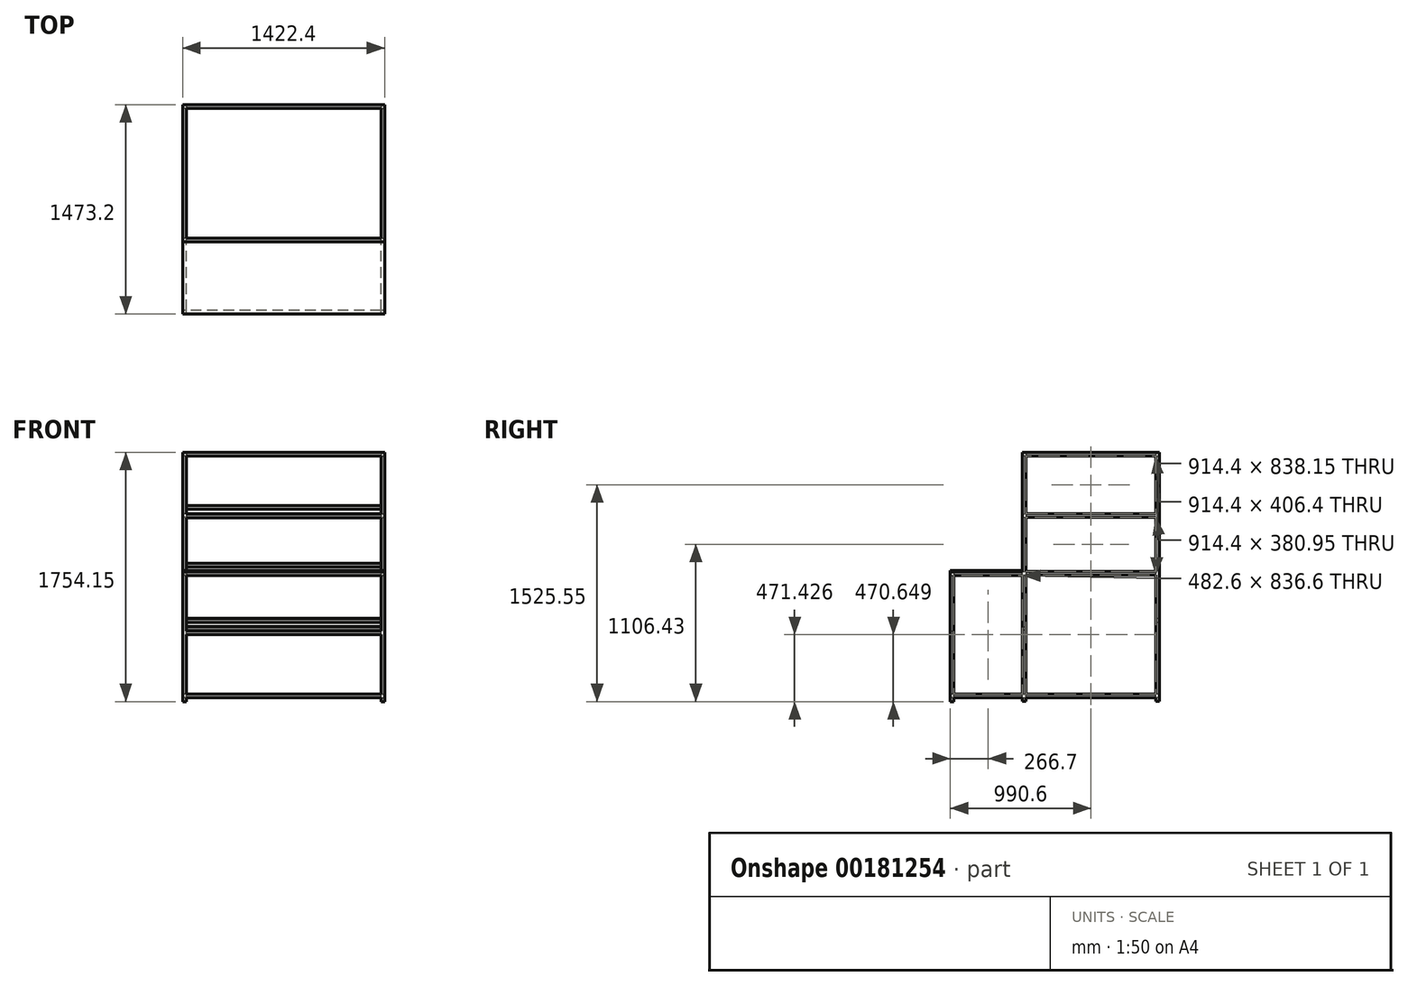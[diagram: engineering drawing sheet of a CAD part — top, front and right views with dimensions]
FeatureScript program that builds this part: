
annotation { "Feature Type Name" : "Feature", "Feature Type Description" : "" }
export const myFeature = defineFeature(function(context is Context, id is Id, definition is map)
    precondition{}
    {
        {
            var Q0;
            Q0=qCreatedBy(makeId("Top.planeOp"),FACE);
            var sketch = newSketch(context, id + "F0", { "sketchPlane" : qUnion([Q0])});
            skLineSegment(sketch, "E0.bottom", {"start": v(685.8, 457.2) * mm, "end": v(-685.8, 457.2) * mm});
            skLineSegment(sketch, "E0.top", {"start": v(685.8, -457.2) * mm, "end": v(-685.8, -457.2) * mm});
            skLineSegment(sketch, "E0.left", {"start": v(685.8, 457.2) * mm, "end": v(685.8, -457.2) * mm});
            skLineSegment(sketch, "E0.right", {"start": v(-685.8, 457.2) * mm, "end": v(-685.8, -457.2) * mm});
            skPoint(sketch, "E0.middle", {"position": v(0, 0) * mm});
            skLineSegment(sketch, "E1.bottom", {"start": v(711.2, 482.6) * mm, "end": v(-711.2, 482.6) * mm});
            skLineSegment(sketch, "E1.top", {"start": v(711.2, -482.6) * mm, "end": v(-711.2, -482.6) * mm});
            skLineSegment(sketch, "E1.left", {"start": v(711.2, 482.6) * mm, "end": v(711.2, -482.6) * mm});
            skLineSegment(sketch, "E1.right", {"start": v(-711.2, 482.6) * mm, "end": v(-711.2, -482.6) * mm});
            skLineSegment(sketch, "E2.bottom", {"start": v(-685.8, 457.2) * mm, "end": v(-711.2, 457.2) * mm});
            skLineSegment(sketch, "E2.top", {"start": v(-685.8, 482.6) * mm, "end": v(-711.2, 482.6) * mm});
            skLineSegment(sketch, "E2.left", {"start": v(-685.8, 457.2) * mm, "end": v(-685.8, 482.6) * mm});
            skLineSegment(sketch, "E2.right", {"start": v(-711.2, 457.2) * mm, "end": v(-711.2, 482.6) * mm});
            skLineSegment(sketch, "E3.bottom", {"start": v(-685.8, -457.2) * mm, "end": v(-711.2, -457.2) * mm});
            skLineSegment(sketch, "E3.top", {"start": v(-685.8, -482.6) * mm, "end": v(-711.2, -482.6) * mm});
            skLineSegment(sketch, "E3.left", {"start": v(-685.8, -457.2) * mm, "end": v(-685.8, -482.6) * mm});
            skLineSegment(sketch, "E3.right", {"start": v(-711.2, -457.2) * mm, "end": v(-711.2, -482.6) * mm});
            skLineSegment(sketch, "E4.bottom", {"start": v(685.8, -457.2) * mm, "end": v(711.2, -457.2) * mm});
            skLineSegment(sketch, "E4.top", {"start": v(685.8, -482.6) * mm, "end": v(711.2, -482.6) * mm});
            skLineSegment(sketch, "E4.left", {"start": v(685.8, -457.2) * mm, "end": v(685.8, -482.6) * mm});
            skLineSegment(sketch, "E4.right", {"start": v(711.2, -457.2) * mm, "end": v(711.2, -482.6) * mm});
            skLineSegment(sketch, "E5.bottom", {"start": v(685.8, 457.2) * mm, "end": v(711.2, 457.2) * mm});
            skLineSegment(sketch, "E5.top", {"start": v(685.8, 482.6) * mm, "end": v(711.2, 482.6) * mm});
            skLineSegment(sketch, "E5.left", {"start": v(685.8, 457.2) * mm, "end": v(685.8, 482.6) * mm});
            skLineSegment(sketch, "E5.right", {"start": v(711.2, 457.2) * mm, "end": v(711.2, 482.6) * mm});
            skSolve(sketch);
        }
        {
            var Q0;
            Q0 = qSketchRegion(id + "F0", true);
            extrude(context, id + "F1", {"entities" : qUnion([Q0]), "depth" : 25.4 * mm});
        }
        {
            var Q0;
            Q0=makeQuery(id+"F0.imprint","IMPRINT",FACE,{"disambiguationData":[TD([[makeQuery(id+"F0.imprint","IMPRINT",EDGE,{"derivedFrom":sQuery(id+"F0.wireOp",EDGE,"E3.bottom")}),1.0]])]});
            var Q1;
            Q1=makeQuery(id+"F0.imprint","IMPRINT",FACE,{"disambiguationData":[TD([[makeQuery(id+"F0.imprint","IMPRINT",EDGE,{"derivedFrom":sQuery(id+"F0.wireOp",EDGE,"E2.bottom")}),-1.0]])]});
            var Q2;
            Q2=makeQuery(id+"F0.imprint","IMPRINT",FACE,{"disambiguationData":[TD([[makeQuery(id+"F0.imprint","IMPRINT",EDGE,{"derivedFrom":sQuery(id+"F0.wireOp",EDGE,"E5.bottom")}),1.0]])]});
            var Q3;
            Q3=makeQuery(id+"F0.imprint","IMPRINT",FACE,{"disambiguationData":[TD([[makeQuery(id+"F0.imprint","IMPRINT",EDGE,{"derivedFrom":sQuery(id+"F0.wireOp",EDGE,"E4.bottom")}),-1.0]])]});
            extrude(context, id + "F2", {"entities" : qUnion([Q0, Q1, Q2, Q3]), "operationType" : NewBodyOperationType.ADD, "oppositeDirection" : true, "depth" : 1727.2 * mm});
        }
        {
            var Q0;
            {var subQ0=sQuery(id+"F0.wireOp",EDGE,"E5.right");var subQ1=sQuery(id+"F0.wireOp",EDGE,"E4.right");Q0=makeQuery(id+"F2.boolean.opBoolean","MERGE",FACE,{"derivedFrom":[makeQuery(id+"F1.opExtrude","SWEPT_FACE",FACE,{"disambiguationData":[OSD([sQuery(id+"F0.wireOp",EDGE,"E1.left"),subQ1,subQ0])]}),makeQuery(id+"F2.opExtrude","SWEPT_FACE",FACE,{"disambiguationData":[OSD([subQ1])]}),makeQuery(id+"F2.opExtrude","SWEPT_FACE",FACE,{"disambiguationData":[OSD([subQ0])]})]});}
            var sketch = newSketch(context, id + "F3", { "sketchPlane" : qUnion([Q0])});
            skLineSegment(sketch, "E6", {"start": v(-457.2, 0) * mm, "end": v(-457.2, -406.4) * mm});
            skLineSegment(sketch, "E7", {"start": v(-457.2, -406.4) * mm, "end": v(457.2, -350.47) * mm});
            skLineSegment(sketch, "E8", {"start": v(-457.2, 0) * mm, "end": v(457.2, 0) * mm});
            skLineSegment(sketch, "E9", {"start": v(-457.2, -406.4) * mm, "end": v(-482.6, -407.95) * mm});
            skLineSegment(sketch, "E10", {"start": v(-482.6, -407.95) * mm, "end": v(-482.6, -433.4) * mm});
            skLineSegment(sketch, "E11", {"start": v(-482.6, -433.4) * mm, "end": v(457.2, -375.92) * mm});
            skLineSegment(sketch, "E12", {"start": v(457.2, -375.92) * mm, "end": v(482.6, -374.37) * mm});
            skLineSegment(sketch, "E13", {"start": v(457.2, -350.47) * mm, "end": v(482.6, -348.92) * mm});
            skLineSegment(sketch, "E14", {"start": v(482.6, -348.92) * mm, "end": v(482.6, -374.37) * mm});
            skLineSegment(sketch, "E15.1.0.0", {"start": v(-457.2, -812.8) * mm, "end": v(457.2, -756.87) * mm});
            skLineSegment(sketch, "E15.1.0.1", {"start": v(-482.6, -839.8) * mm, "end": v(457.2, -782.32) * mm});
            skLineSegment(sketch, "E15.1.0.2", {"start": v(457.2, -782.32) * mm, "end": v(482.6, -780.77) * mm});
            skLineSegment(sketch, "E15.1.0.3", {"start": v(482.6, -755.32) * mm, "end": v(482.6, -780.77) * mm});
            skLineSegment(sketch, "E15.1.0.4", {"start": v(-482.6, -814.35) * mm, "end": v(-482.6, -839.8) * mm});
            skLineSegment(sketch, "E15.1.0.5", {"start": v(-457.2, -812.8) * mm, "end": v(-482.6, -814.35) * mm});
            skLineSegment(sketch, "E15.1.0.6", {"start": v(457.2, -756.87) * mm, "end": v(482.6, -755.32) * mm});
            skLineSegment(sketch, "E15.direction1", {"start": v(-482.6, -433.4) * mm, "end": v(-482.6, -839.8) * mm, "construction": true});
            skSolve(sketch);
        }
        {
            var Q0;
            {var subQ0=sQuery(id+"F3.wireOp",EDGE,"E9");Q0=makeQuery(id+"F3.imprint","IMPRINT",FACE,{"disambiguationData":[TD([[makeQuery(id+"F3.imprint","IMPRINT",EDGE,{"derivedFrom":subQ0}),1.0]])]});}
            var Q1;
            {var subQ0=sQuery(id+"F3.wireOp",EDGE,"E12");Q1=makeQuery(id+"F3.imprint","IMPRINT",FACE,{"disambiguationData":[TD([[makeQuery(id+"F3.imprint","IMPRINT",EDGE,{"derivedFrom":subQ0}),1.0]])]});}
            var Q2;
            {var subQ0=sQuery(id+"F3.wireOp",EDGE,"E15.1.0.2");Q2=makeQuery(id+"F3.imprint","IMPRINT",FACE,{"disambiguationData":[TD([[makeQuery(id+"F3.imprint","IMPRINT",EDGE,{"derivedFrom":subQ0}),1.0]])]});}
            var Q3;
            {var subQ0=sQuery(id+"F3.wireOp",EDGE,"E15.1.0.4");Q3=makeQuery(id+"F3.imprint","IMPRINT",FACE,{"disambiguationData":[TD([[makeQuery(id+"F3.imprint","IMPRINT",EDGE,{"derivedFrom":subQ0}),1.0]])]});}
            extrude(context, id + "F4", {"entities" : qUnion([Q0, Q1, Q2, Q3]), "operationType" : NewBodyOperationType.ADD, "oppositeDirection" : true, "depth" : 1422.4 * mm});
        }
        {
            var Q0;
            Q0=qCreatedBy(makeId("Top.planeOp"),FACE);
            cPlane(context, id + "F5", {"entities" : qUnion([Q0]), "cplaneType" : CPlaneType.OFFSET, "offset" : 1676.4 * mm, "oppositeDirection" : true, "width" : 152.4 * mm, "height" : 152.4 * mm});
        }
        {
            var Q0;
            Q0=qCreatedBy(id+"F5.planeOp",FACE);
            var sketch = newSketch(context, id + "F6", { "sketchPlane" : qUnion([Q0])});
            skLineSegment(sketch, "E16.bottom", {"start": v(-711.2, -482.6) * mm, "end": v(711.2, -482.6) * mm});
            skLineSegment(sketch, "E16.top", {"start": v(-711.2, 482.6) * mm, "end": v(711.2, 482.6) * mm});
            skLineSegment(sketch, "E16.left", {"start": v(-711.2, -482.6) * mm, "end": v(-711.2, 482.6) * mm});
            skLineSegment(sketch, "E16.right", {"start": v(711.2, -482.6) * mm, "end": v(711.2, 482.6) * mm});
            skPoint(sketch, "E16.middle", {"position": v(0, 0) * mm});
            skLineSegment(sketch, "E17.bottom", {"start": v(-685.8, -457.2) * mm, "end": v(685.8, -457.2) * mm});
            skLineSegment(sketch, "E17.top", {"start": v(-685.8, 457.2) * mm, "end": v(685.8, 457.2) * mm});
            skLineSegment(sketch, "E17.left", {"start": v(-685.8, -457.2) * mm, "end": v(-685.8, 457.2) * mm});
            skLineSegment(sketch, "E17.right", {"start": v(685.8, -457.2) * mm, "end": v(685.8, 457.2) * mm});
            skSolve(sketch);
        }
        {
            var Q0;
            Q0 = qSketchRegion(id + "F6", true);
            extrude(context, id + "F7", {"entities" : qUnion([Q0]), "operationType" : NewBodyOperationType.ADD, "oppositeDirection" : true, "depth" : 25.4 * mm});
        }
        {
            var Q0;
            {var subQ2=sQuery(id+"F3.wireOp",EDGE,"E11");var subQ7=sQuery(id+"F0.wireOp",EDGE,"E4.right");var subQ8=sQuery(id+"F0.wireOp",EDGE,"E1.left");var subQ11=sQuery(id+"F0.wireOp",EDGE,"E0.top");var subQ14=sQuery(id+"F3.wireOp",EDGE,"E15.1.0.1");var subQ18=sQuery(id+"F0.wireOp",EDGE,"E4.bottom");var subQ19=makeQuery(id+"F2.opExtrude","SWEPT_EDGE",EDGE,{"disambiguationData":[OSD([subQ8,subQ18,subQ7])]});Q0=makeQuery(id+"F7.boolean.opBoolean","SPLIT",FACE,{"disambiguationData":[TD([makeQuery(id+"F1.opExtrude","SWEPT_FACE",FACE,{"disambiguationData":[OSD([subQ11])]})])],"derivedFrom":makeQuery(id+"F4.boolean.opBoolean","MERGE",FACE,{"derivedFrom":[makeQuery(id+"F2.opExtrude","SWEPT_FACE",FACE,{"disambiguationData":[OSD([sQuery(id+"F0.wireOp",EDGE,"E3.bottom")])]}),makeQuery(id+"F2.opExtrude","SWEPT_FACE",FACE,{"disambiguationData":[OSD([subQ18])]}),makeQuery(id+"F4.opExtrude","SWEPT_FACE",FACE,{"disambiguationData":[OSD([subQ8,subQ18,subQ7]),TDD([makeQuery(id+"F3.imprint","IMPRINT",EDGE,{"disambiguationData":[TD([[makeQuery(id+"F3.imprint","INTERSECT",VERTEX,{"derivedFrom":[subQ19,subQ2]}),-1.0]])],"derivedFrom":subQ19})])]}),makeQuery(id+"F4.opExtrude","SWEPT_FACE",FACE,{"disambiguationData":[OSD([subQ8,subQ18,subQ7]),TDD([makeQuery(id+"F3.imprint","IMPRINT",EDGE,{"disambiguationData":[TD([[makeQuery(id+"F3.imprint","INTERSECT",VERTEX,{"derivedFrom":[subQ19,subQ14]}),-1.0]])],"derivedFrom":subQ19})])]})]})});}
            var sketch = newSketch(context, id + "F8", { "sketchPlane" : qUnion([Q0])});
            skLineSegment(sketch, "E18.bottom", {"start": v(-685.8, -812.8) * mm, "end": v(-711.2, -812.8) * mm});
            skLineSegment(sketch, "E18.top", {"start": v(-685.8, -838.25) * mm, "end": v(-711.2, -838.25) * mm});
            skLineSegment(sketch, "E18.left", {"start": v(-685.8, -812.8) * mm, "end": v(-685.8, -838.25) * mm});
            skLineSegment(sketch, "E18.right", {"start": v(-711.2, -812.8) * mm, "end": v(-711.2, -838.25) * mm});
            skLineSegment(sketch, "E19.bottom", {"start": v(685.8, -812.8) * mm, "end": v(711.2, -812.8) * mm});
            skLineSegment(sketch, "E19.top", {"start": v(685.8, -838.25) * mm, "end": v(711.2, -838.25) * mm});
            skLineSegment(sketch, "E19.left", {"start": v(685.8, -812.8) * mm, "end": v(685.8, -838.25) * mm});
            skLineSegment(sketch, "E19.right", {"start": v(711.2, -812.8) * mm, "end": v(711.2, -838.25) * mm});
            skLineSegment(sketch, "E20.bottom", {"start": v(-685.8, -406.4) * mm, "end": v(-711.2, -406.4) * mm});
            skLineSegment(sketch, "E20.top", {"start": v(-685.8, -431.85) * mm, "end": v(-711.2, -431.85) * mm});
            skLineSegment(sketch, "E20.left", {"start": v(-685.8, -406.4) * mm, "end": v(-685.8, -431.85) * mm});
            skLineSegment(sketch, "E20.right", {"start": v(-711.2, -406.4) * mm, "end": v(-711.2, -431.85) * mm});
            skLineSegment(sketch, "E21.bottom", {"start": v(685.8, -406.4) * mm, "end": v(711.2, -406.4) * mm});
            skLineSegment(sketch, "E21.top", {"start": v(685.8, -431.85) * mm, "end": v(711.2, -431.85) * mm});
            skLineSegment(sketch, "E21.left", {"start": v(685.8, -406.4) * mm, "end": v(685.8, -431.85) * mm});
            skLineSegment(sketch, "E21.right", {"start": v(711.2, -406.4) * mm, "end": v(711.2, -431.85) * mm});
            skSolve(sketch);
        }
        {
            var Q0;
            Q0 = qSketchRegion(id + "F8", true);
            extrude(context, id + "F9", {"entities" : qUnion([Q0]), "operationType" : NewBodyOperationType.ADD, "depth" : 914.4 * mm});
        }
        {
            var Q0;
            {var subQ0=sQuery(id+"F0.wireOp",EDGE,"E4.top");var subQ1=sQuery(id+"F0.wireOp",EDGE,"E3.top");Q0=makeQuery(id+"F7.boolean.opBoolean","MERGE",FACE,{"derivedFrom":[makeQuery(id+"F4.boolean.opBoolean","MERGE",FACE,{"derivedFrom":[makeQuery(id+"F2.boolean.opBoolean","MERGE",FACE,{"derivedFrom":[makeQuery(id+"F1.opExtrude","SWEPT_FACE",FACE,{"disambiguationData":[OSD([sQuery(id+"F0.wireOp",EDGE,"E1.top"),subQ1,subQ0])]}),makeQuery(id+"F2.opExtrude","SWEPT_FACE",FACE,{"disambiguationData":[OSD([subQ1])]}),makeQuery(id+"F2.opExtrude","SWEPT_FACE",FACE,{"disambiguationData":[OSD([subQ0])]})]}),makeQuery(id+"F4.opExtrude","SWEPT_FACE",FACE,{"disambiguationData":[OSD([sQuery(id+"F3.wireOp",EDGE,"E10")])]}),makeQuery(id+"F4.opExtrude","SWEPT_FACE",FACE,{"disambiguationData":[OSD([sQuery(id+"F3.wireOp",EDGE,"E15.1.0.4")])]})]}),makeQuery(id+"F7.opExtrude","SWEPT_FACE",FACE,{"disambiguationData":[OSD([sQuery(id+"F6.wireOp",EDGE,"E16.bottom")])]})]});}
            var sketch = newSketch(context, id + "F10", { "sketchPlane" : qUnion([Q0])});
            skLineSegment(sketch, "E22.bottom", {"start": v(-685.8, -839.8) * mm, "end": v(-711.2, -839.8) * mm});
            skLineSegment(sketch, "E22.top", {"start": v(-685.8, -814.35) * mm, "end": v(-711.2, -814.35) * mm});
            skLineSegment(sketch, "E22.left", {"start": v(-685.8, -839.8) * mm, "end": v(-685.8, -814.35) * mm});
            skLineSegment(sketch, "E22.right", {"start": v(-711.2, -839.8) * mm, "end": v(-711.2, -814.35) * mm});
            skLineSegment(sketch, "E23.bottom", {"start": v(685.8, -839.8) * mm, "end": v(711.2, -839.8) * mm});
            skLineSegment(sketch, "E23.top", {"start": v(685.8, -814.35) * mm, "end": v(711.2, -814.35) * mm});
            skLineSegment(sketch, "E23.left", {"start": v(685.8, -839.8) * mm, "end": v(685.8, -814.35) * mm});
            skLineSegment(sketch, "E23.right", {"start": v(711.2, -839.8) * mm, "end": v(711.2, -814.35) * mm});
            skLineSegment(sketch, "E24.bottom", {"start": v(-685.8, -1701.8) * mm, "end": v(-711.2, -1701.8) * mm});
            skLineSegment(sketch, "E24.top", {"start": v(-685.8, -1676.4) * mm, "end": v(-711.2, -1676.4) * mm});
            skLineSegment(sketch, "E24.left", {"start": v(-685.8, -1701.8) * mm, "end": v(-685.8, -1676.4) * mm});
            skLineSegment(sketch, "E24.right", {"start": v(-711.2, -1701.8) * mm, "end": v(-711.2, -1676.4) * mm});
            skLineSegment(sketch, "E25.bottom", {"start": v(685.8, -1701.8) * mm, "end": v(711.2, -1701.8) * mm});
            skLineSegment(sketch, "E25.top", {"start": v(685.8, -1676.4) * mm, "end": v(711.2, -1676.4) * mm});
            skLineSegment(sketch, "E25.left", {"start": v(685.8, -1701.8) * mm, "end": v(685.8, -1676.4) * mm});
            skLineSegment(sketch, "E25.right", {"start": v(711.2, -1701.8) * mm, "end": v(711.2, -1676.4) * mm});
            skSolve(sketch);
        }
        {
            var Q0;
            Q0 = qSketchRegion(id + "F10", true);
            extrude(context, id + "F11", {"entities" : qUnion([Q0]), "operationType" : NewBodyOperationType.ADD, "depth" : 508 * mm});
        }
        {
            var Q0;
            Q0=makeQuery(id+"F11.opExtrude","SWEPT_FACE",FACE,{"disambiguationData":[OSD([sQuery(id+"F10.wireOp",EDGE,"E22.top")])]});
            var sketch = newSketch(context, id + "F12", { "sketchPlane" : qUnion([Q0])});
            skLineSegment(sketch, "E26.bottom", {"start": v(-711.2, -990.6) * mm, "end": v(-685.8, -990.6) * mm});
            skLineSegment(sketch, "E26.top", {"start": v(-711.2, -965.2) * mm, "end": v(-685.8, -965.2) * mm});
            skLineSegment(sketch, "E26.left", {"start": v(-711.2, -990.6) * mm, "end": v(-711.2, -965.2) * mm});
            skLineSegment(sketch, "E26.right", {"start": v(-685.8, -990.6) * mm, "end": v(-685.8, -965.2) * mm});
            skSolve(sketch);
        }
        {
            var Q0;
            Q0 = qSketchRegion(id + "F12", true);
            var Q1;
            Q1 = qSketchRegion(id + "F14", true);
            extrude(context, id + "F13", {"entities" : qUnion([Q0, Q1]), "operationType" : NewBodyOperationType.ADD, "oppositeDirection" : true, "depth" : 914.4 * mm});
        }
        {
            var Q0;
            Q0=makeQuery(id+"F11.opExtrude","SWEPT_FACE",FACE,{"disambiguationData":[OSD([sQuery(id+"F10.wireOp",EDGE,"E23.top")])]});
            var sketch = newSketch(context, id + "F14", { "sketchPlane" : qUnion([Q0])});
            skLineSegment(sketch, "E27.bottom", {"start": v(711.2, -990.6) * mm, "end": v(685.8, -990.6) * mm});
            skLineSegment(sketch, "E27.top", {"start": v(711.2, -965.2) * mm, "end": v(685.8, -965.2) * mm});
            skLineSegment(sketch, "E27.left", {"start": v(711.2, -990.6) * mm, "end": v(711.2, -965.2) * mm});
            skLineSegment(sketch, "E27.right", {"start": v(685.8, -990.6) * mm, "end": v(685.8, -965.2) * mm});
            skSolve(sketch);
        }
        {
            var Q0;
            Q0=makeQuery(id+"F14.imprint","IMPRINT",FACE,{"disambiguationData":[TD([[makeQuery(id+"F14.imprint","IMPRINT",EDGE,{"derivedFrom":sQuery(id+"F14.wireOp",EDGE,"E27.bottom")}),1.0]])]});
            extrude(context, id + "F15", {"entities" : qUnion([Q0]), "operationType" : NewBodyOperationType.ADD, "oppositeDirection" : true, "depth" : 914.4 * mm});
        }
        {
            var Q0;
            Q0=makeQuery(id+"F13.boolean.opBoolean","MERGE",FACE,{"derivedFrom":[makeQuery(id+"F11.opExtrude","SWEPT_FACE",FACE,{"disambiguationData":[OSD([sQuery(id+"F10.wireOp",EDGE,"E22.left")])]}),makeQuery(id+"F11.opExtrude","SWEPT_FACE",FACE,{"disambiguationData":[OSD([sQuery(id+"F10.wireOp",EDGE,"E24.left")])]}),makeQuery(id+"F13.opExtrude","SWEPT_FACE",FACE,{"disambiguationData":[OSD([sQuery(id+"F12.wireOp",EDGE,"E26.right")])]})]});
            var sketch = newSketch(context, id + "F16", { "sketchPlane" : qUnion([Q0])});
            skLineSegment(sketch, "E28.bottom", {"start": v(-990.6, -814.35) * mm, "end": v(-965.2, -814.35) * mm});
            skLineSegment(sketch, "E28.top", {"start": v(-990.6, -839.8) * mm, "end": v(-965.2, -839.8) * mm});
            skLineSegment(sketch, "E28.left", {"start": v(-990.6, -814.35) * mm, "end": v(-990.6, -839.8) * mm});
            skLineSegment(sketch, "E28.right", {"start": v(-965.2, -814.35) * mm, "end": v(-965.2, -839.8) * mm});
            skLineSegment(sketch, "E29.bottom", {"start": v(-965.2, -1701.8) * mm, "end": v(-990.6, -1701.8) * mm});
            skLineSegment(sketch, "E29.top", {"start": v(-965.2, -1676.4) * mm, "end": v(-990.6, -1676.4) * mm});
            skLineSegment(sketch, "E29.left", {"start": v(-965.2, -1701.8) * mm, "end": v(-965.2, -1676.4) * mm});
            skLineSegment(sketch, "E29.right", {"start": v(-990.6, -1701.8) * mm, "end": v(-990.6, -1676.4) * mm});
            skSolve(sketch);
        }
        {
            var Q0;
            Q0 = qSketchRegion(id + "F16", true);
            extrude(context, id + "F17", {"entities" : qUnion([Q0]), "operationType" : NewBodyOperationType.ADD, "depth" : 1371.6 * mm});
        }
        {
            var Q0;
            Q0=makeQuery(id+"F17.boolean.opBoolean","MERGE",FACE,{"derivedFrom":[makeQuery(id+"F11.opExtrude","SWEPT_FACE",FACE,{"disambiguationData":[OSD([sQuery(id+"F10.wireOp",EDGE,"E22.top")])]}),makeQuery(id+"F11.opExtrude","SWEPT_FACE",FACE,{"disambiguationData":[OSD([sQuery(id+"F10.wireOp",EDGE,"E23.top")])]}),makeQuery(id+"F17.opExtrude","SWEPT_FACE",FACE,{"disambiguationData":[OSD([sQuery(id+"F16.wireOp",EDGE,"E28.bottom")])]})]});
            var sketch = newSketch(context, id + "F18", { "sketchPlane" : qUnion([Q0])});
            skLineSegment(sketch, "E30.bottom", {"start": v(-711.2, -990.6) * mm, "end": v(711.2, -990.6) * mm});
            skLineSegment(sketch, "E30.top", {"start": v(-711.2, -482.6) * mm, "end": v(711.2, -482.6) * mm});
            skLineSegment(sketch, "E30.left", {"start": v(-711.2, -990.6) * mm, "end": v(-711.2, -482.6) * mm});
            skLineSegment(sketch, "E30.right", {"start": v(711.2, -990.6) * mm, "end": v(711.2, -482.6) * mm});
            skSolve(sketch);
        }
        {
            var Q0;
            Q0 = qSketchRegion(id + "F18", true);
            extrude(context, id + "F19", {"entities" : qUnion([Q0]), "depth" : 9.52 * mm});
        }
        {
            var Q0;
            {var subQ0=sQuery(id+"F0.wireOp",EDGE,"E5.right");var subQ1=sQuery(id+"F0.wireOp",EDGE,"E4.right");Q0=makeQuery(id+"F15.boolean.opBoolean","MERGE",FACE,{"derivedFrom":[makeQuery(id+"F11.boolean.opBoolean","MERGE",FACE,{"derivedFrom":[makeQuery(id+"F9.boolean.opBoolean","MERGE",FACE,{"derivedFrom":[makeQuery(id+"F7.boolean.opBoolean","MERGE",FACE,{"derivedFrom":[makeQuery(id+"F2.boolean.opBoolean","MERGE",FACE,{"derivedFrom":[makeQuery(id+"F1.opExtrude","SWEPT_FACE",FACE,{"disambiguationData":[OSD([sQuery(id+"F0.wireOp",EDGE,"E1.left"),subQ1,subQ0])]}),makeQuery(id+"F2.opExtrude","SWEPT_FACE",FACE,{"disambiguationData":[OSD([subQ1])]}),makeQuery(id+"F2.opExtrude","SWEPT_FACE",FACE,{"disambiguationData":[OSD([subQ0])]})]}),makeQuery(id+"F7.opExtrude","SWEPT_FACE",FACE,{"disambiguationData":[OSD([sQuery(id+"F6.wireOp",EDGE,"E16.right")])]})]}),makeQuery(id+"F9.opExtrude","SWEPT_FACE",FACE,{"disambiguationData":[OSD([sQuery(id+"F8.wireOp",EDGE,"E18.right")])]}),makeQuery(id+"F9.opExtrude","SWEPT_FACE",FACE,{"disambiguationData":[OSD([sQuery(id+"F8.wireOp",EDGE,"E20.right")])]})]}),makeQuery(id+"F11.opExtrude","SWEPT_FACE",FACE,{"disambiguationData":[OSD([sQuery(id+"F10.wireOp",EDGE,"E23.right")])]}),makeQuery(id+"F11.opExtrude","SWEPT_FACE",FACE,{"disambiguationData":[OSD([sQuery(id+"F10.wireOp",EDGE,"E25.right")])]})]}),makeQuery(id+"F15.opExtrude","SWEPT_FACE",FACE,{"disambiguationData":[OSD([sQuery(id+"F14.wireOp",EDGE,"E27.left")])]})]});}
            var sketch = newSketch(context, id + "F20", { "sketchPlane" : qUnion([Q0])});
            skLineSegment(sketch, "E31", {"start": v(482.6, -838.25) * mm, "end": v(482.6, -1143.05) * mm});
            skLineSegment(sketch, "E32", {"start": v(482.6, -1143.05) * mm, "end": v(-990.6, -1233.15) * mm});
            skLineSegment(sketch, "E33", {"start": v(-990.6, -1233.15) * mm, "end": v(-990.6, -1258.55) * mm});
            skLineSegment(sketch, "E34", {"start": v(-990.6, -1258.55) * mm, "end": v(482.6, -1168.45) * mm});
            skLineSegment(sketch, "E35", {"start": v(482.6, -1168.45) * mm, "end": v(482.6, -1143.05) * mm});
            skLineSegment(sketch, "E36", {"start": v(457.2, -838.25) * mm, "end": v(326.37, -838.25) * mm});
            skLineSegment(sketch, "E37", {"start": v(-965.2, -1231.6) * mm, "end": v(-965.2, -1257) * mm});
            skLineSegment(sketch, "E38", {"start": v(-482.6, -1202.08) * mm, "end": v(-482.6, -1227.48) * mm});
            skLineSegment(sketch, "E39", {"start": v(-457.2, -1200.53) * mm, "end": v(-457.2, -1225.93) * mm});
            skLineSegment(sketch, "E40", {"start": v(457.2, -1144.6) * mm, "end": v(457.2, -1170) * mm});
            skLineSegment(sketch, "E41.direction1", {"start": v(-990.6, -1233.15) * mm, "end": v(-990.6, -1588.75) * mm, "construction": true});
            skSolve(sketch);
        }
        {
            var Q0;
            {var subQ0=sQuery(id+"F20.wireOp",EDGE,"E33");Q0=makeQuery(id+"F20.imprint","IMPRINT",FACE,{"disambiguationData":[TD([[makeQuery(id+"F20.imprint","IMPRINT",EDGE,{"derivedFrom":subQ0}),1.0]])]});}
            var Q1;
            {var subQ0=sQuery(id+"F20.wireOp",EDGE,"E38");Q1=makeQuery(id+"F20.imprint","IMPRINT",FACE,{"disambiguationData":[TD([[makeQuery(id+"F20.imprint","IMPRINT",EDGE,{"derivedFrom":subQ0}),1.0]])]});}
            var Q2;
            {var subQ0=sQuery(id+"F20.wireOp",EDGE,"E35");Q2=makeQuery(id+"F20.imprint","IMPRINT",FACE,{"disambiguationData":[TD([[makeQuery(id+"F20.imprint","IMPRINT",EDGE,{"derivedFrom":subQ0}),-1.0]])]});}
            var Q3;
            {var subQ5=sQuery(id+"F20.wireOp",EDGE,"E41.1.0.5");Q3=makeQuery(id+"F20.imprint","IMPRINT",FACE,{"disambiguationData":[TD([[makeQuery(id+"F20.imprint","IMPRINT",EDGE,{"derivedFrom":subQ5}),-1.0]])]});}
            var Q4;
            {var subQ0=sQuery(id+"F20.wireOp",EDGE,"E41.1.0.3");Q4=makeQuery(id+"F20.imprint","IMPRINT",FACE,{"disambiguationData":[TD([[makeQuery(id+"F20.imprint","IMPRINT",EDGE,{"derivedFrom":subQ0}),1.0]])]});}
            var Q5;
            {var subQ6=sQuery(id+"F20.wireOp",EDGE,"E41.1.0.2");Q5=makeQuery(id+"F20.imprint","IMPRINT",FACE,{"disambiguationData":[TD([[makeQuery(id+"F20.imprint","IMPRINT",EDGE,{"derivedFrom":subQ6}),1.0]])]});}
            extrude(context, id + "F21", {"entities" : qUnion([Q0, Q1, Q2, Q3, Q4, Q5]), "operationType" : NewBodyOperationType.ADD, "oppositeDirection" : true, "depth" : 1422.4 * mm});
        }
    });
